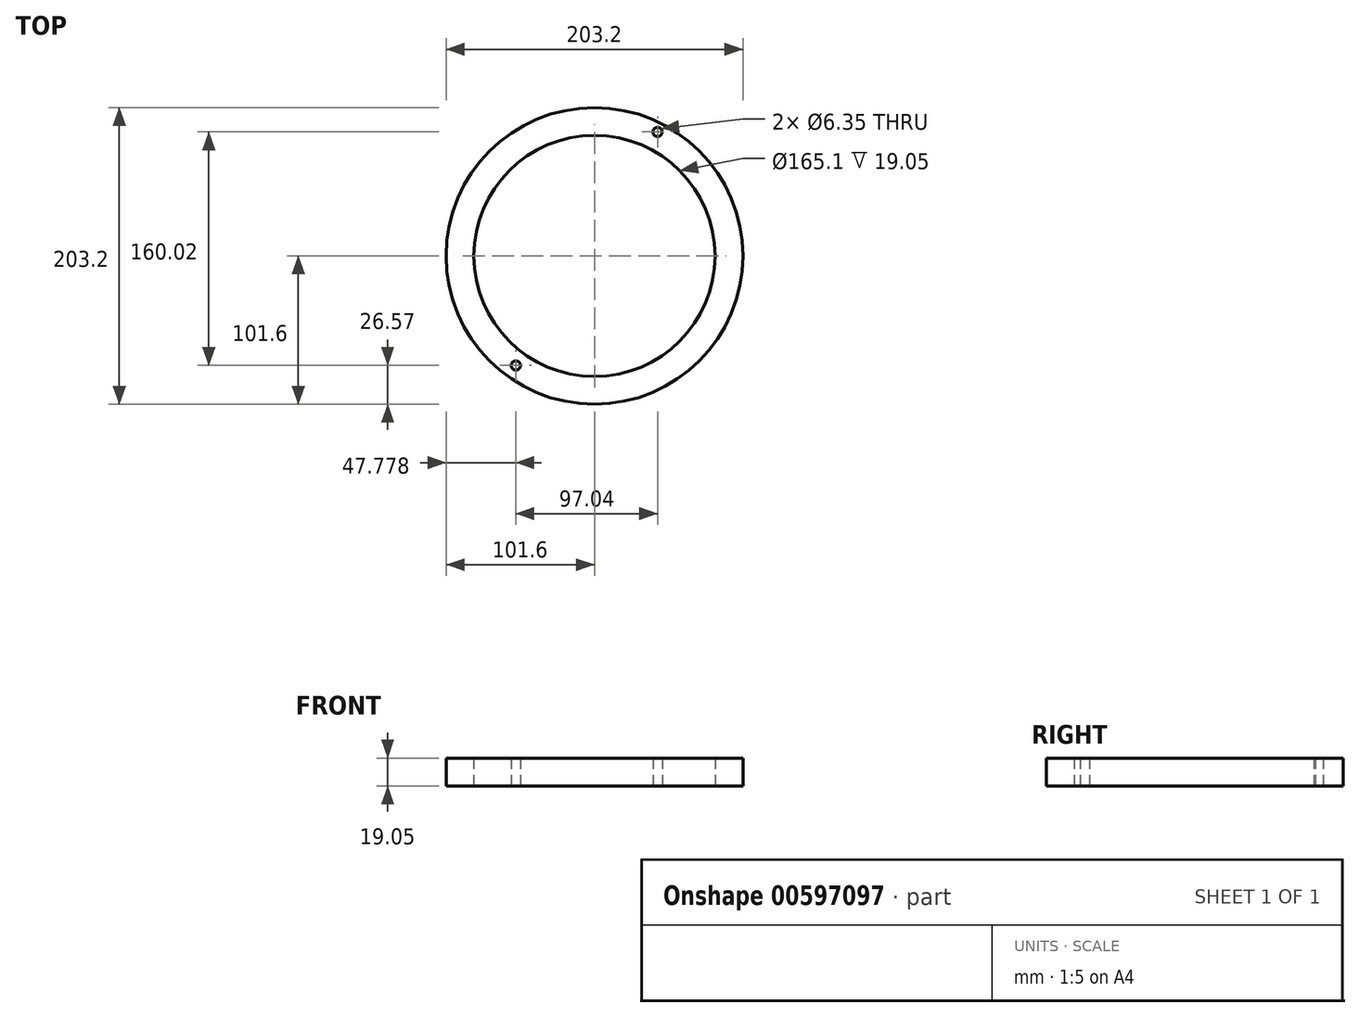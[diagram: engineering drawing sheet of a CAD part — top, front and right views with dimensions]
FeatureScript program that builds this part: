
annotation { "Feature Type Name" : "Feature", "Feature Type Description" : "" }
export const myFeature = defineFeature(function(context is Context, id is Id, definition is map)
    precondition{}
    {
        {
            var Q0;
            Q0=qCreatedBy(makeId("Top.planeOp"),FACE);
            var sketch = newSketch(context, id + "F0", { "sketchPlane" : qUnion([Q0])});
            skCircle(sketch, "E0", {"center": v(0, 0) * mm, "radius": 101.6 * mm});
            skCircle(sketch, "E1.0", {"center": v(0, 0) * mm, "radius": 82.55 * mm});
            skCircle(sketch, "E2", {"center": v(43.22, 85) * mm, "radius": 3.18 * mm});
            skCircle(sketch, "E3", {"center": v(-53.82, -75.03) * mm, "radius": 3.18 * mm});
            skSolve(sketch);
        }
        {
            var Q0;
            Q0=qSketchRegion(id+"F0",true);
            extrude(context, id + "F1", {"entities" : qUnion([Q0]), "depth" : 19.05 * mm, "offsetDistance" : 25.4 * mm});
        }
    });
